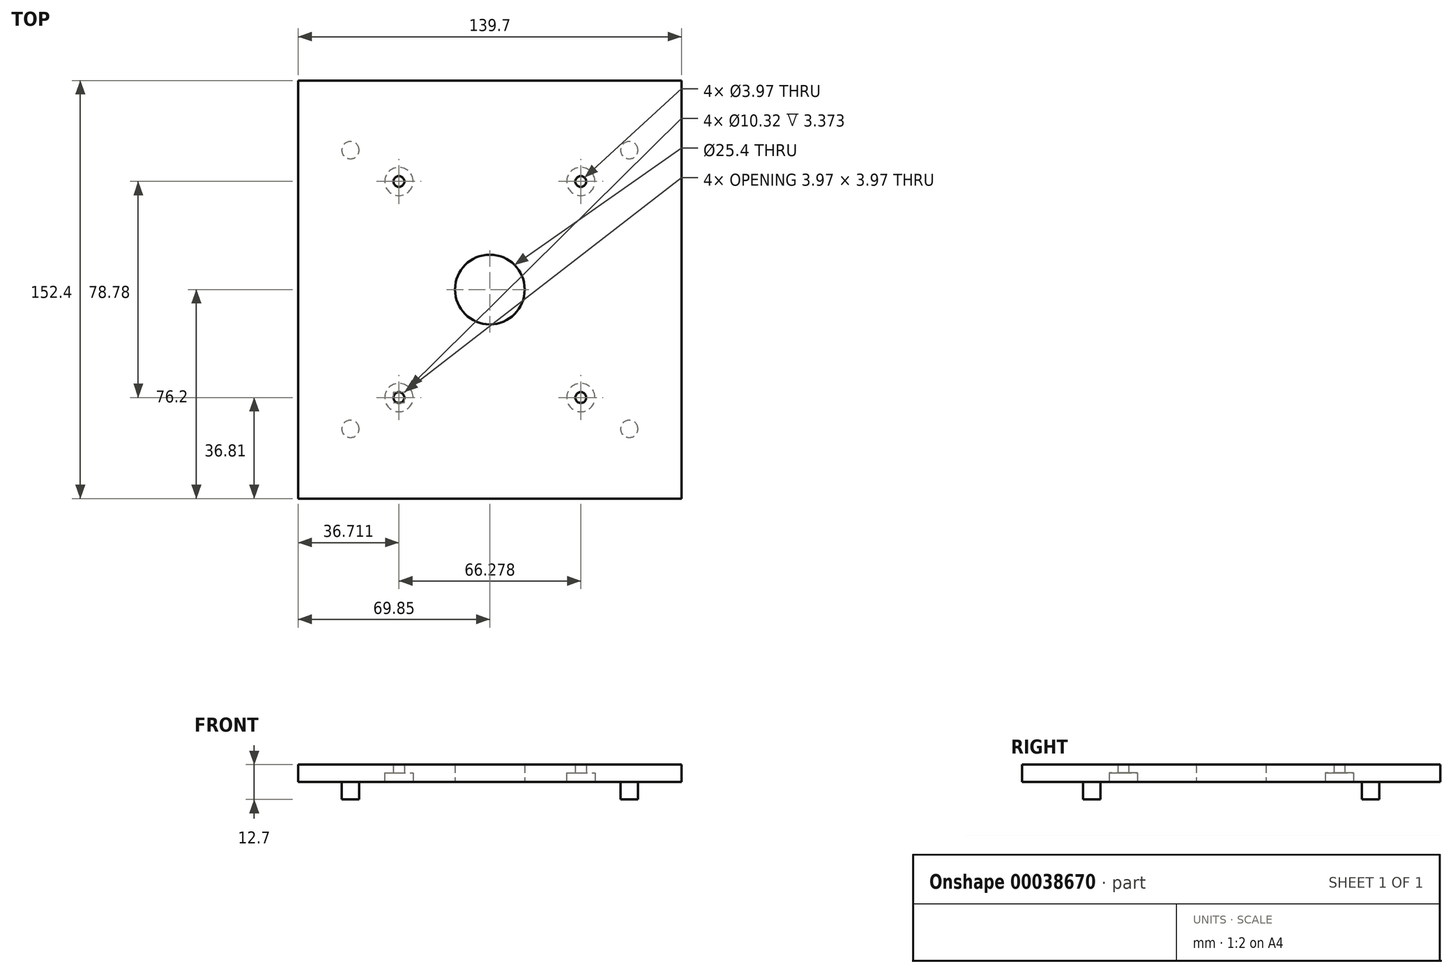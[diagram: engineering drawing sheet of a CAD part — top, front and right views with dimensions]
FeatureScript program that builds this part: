
annotation { "Feature Type Name" : "Feature", "Feature Type Description" : "" }
export const myFeature = defineFeature(function(context is Context, id is Id, definition is map)
    precondition{}
    {
        {
            var Q0;
            Q0=qCreatedBy(makeId("Top.planeOp"),FACE);
            var sketch = newSketch(context, id + "F0", { "sketchPlane" : qUnion([Q0])});
            skLineSegment(sketch, "E0.rect.bottom", {"start": v(33.14, -39.39) * mm, "end": v(-33.14, -39.39) * mm, "construction": true});
            skLineSegment(sketch, "E0.rect.top", {"start": v(33.14, 39.39) * mm, "end": v(-33.14, 39.39) * mm, "construction": true});
            skLineSegment(sketch, "E0.rect.left", {"start": v(33.14, -39.39) * mm, "end": v(33.14, 39.39) * mm, "construction": true});
            skLineSegment(sketch, "E0.rect.right", {"start": v(-33.14, -39.39) * mm, "end": v(-33.14, 39.39) * mm, "construction": true});
            skPoint(sketch, "E0.rect.middle", {"position": v(0, 0) * mm});
            skLineSegment(sketch, "E1.rect.bottom", {"start": v(50.8, 50.8) * mm, "end": v(-50.8, 50.8) * mm, "construction": true});
            skLineSegment(sketch, "E1.rect.top", {"start": v(50.8, -50.8) * mm, "end": v(-50.8, -50.8) * mm, "construction": true});
            skLineSegment(sketch, "E1.rect.left", {"start": v(50.8, 50.8) * mm, "end": v(50.8, -50.8) * mm, "construction": true});
            skLineSegment(sketch, "E1.rect.right", {"start": v(-50.8, 50.8) * mm, "end": v(-50.8, -50.8) * mm, "construction": true});
            skCircle(sketch, "E2", {"center": v(-50.8, 50.8) * mm, "radius": 3.18 * mm});
            skCircle(sketch, "E3", {"center": v(-33.14, -39.39) * mm, "radius": 1.98 * mm});
            skCircle(sketch, "E4", {"center": v(33.14, -39.39) * mm, "radius": 1.98 * mm});
            skCircle(sketch, "E5", {"center": v(-33.14, 39.39) * mm, "radius": 1.98 * mm});
            skCircle(sketch, "E6", {"center": v(0, 0) * mm, "radius": 12.7 * mm});
            skLineSegment(sketch, "E7.rect.bottom", {"start": v(69.85, 76.2) * mm, "end": v(-69.85, 76.2) * mm});
            skLineSegment(sketch, "E7.rect.top", {"start": v(69.85, -76.2) * mm, "end": v(-69.85, -76.2) * mm});
            skLineSegment(sketch, "E7.rect.left", {"start": v(69.85, 76.2) * mm, "end": v(69.85, -76.2) * mm});
            skLineSegment(sketch, "E7.rect.right", {"start": v(-69.85, 76.2) * mm, "end": v(-69.85, -76.2) * mm});
            skCircle(sketch, "E8", {"center": v(33.14, 39.39) * mm, "radius": 1.98 * mm});
            skCircle(sketch, "E9.0.1.0", {"center": v(-50.8, 25.4) * mm, "radius": 3.18 * mm});
            skCircle(sketch, "E9.0.2.0", {"center": v(-50.8, 0) * mm, "radius": 3.18 * mm});
            skCircle(sketch, "E9.0.3.0", {"center": v(-50.8, -25.4) * mm, "radius": 3.18 * mm});
            skCircle(sketch, "E9.0.4.0", {"center": v(-50.8, -50.8) * mm, "radius": 3.18 * mm});
            skCircle(sketch, "E9.1.0.0", {"center": v(-25.4, 50.8) * mm, "radius": 3.18 * mm});
            skCircle(sketch, "E9.1.1.0", {"center": v(-25.4, 25.4) * mm, "radius": 3.18 * mm});
            skCircle(sketch, "E9.1.2.0", {"center": v(-25.4, 0) * mm, "radius": 3.18 * mm});
            skCircle(sketch, "E9.1.3.0", {"center": v(-25.4, -25.4) * mm, "radius": 3.18 * mm});
            skCircle(sketch, "E9.1.4.0", {"center": v(-25.4, -50.8) * mm, "radius": 3.18 * mm});
            skCircle(sketch, "E9.2.0.0", {"center": v(0, 50.8) * mm, "radius": 3.18 * mm});
            skCircle(sketch, "E9.2.1.0", {"center": v(0, 25.4) * mm, "radius": 3.18 * mm});
            skCircle(sketch, "E9.2.2.0", {"center": v(0, 0) * mm, "radius": 3.18 * mm});
            skCircle(sketch, "E9.2.3.0", {"center": v(0, -25.4) * mm, "radius": 3.18 * mm});
            skCircle(sketch, "E9.2.4.0", {"center": v(0, -50.8) * mm, "radius": 3.18 * mm});
            skCircle(sketch, "E9.3.0.0", {"center": v(25.4, 50.8) * mm, "radius": 3.18 * mm});
            skCircle(sketch, "E9.3.1.0", {"center": v(25.4, 25.4) * mm, "radius": 3.18 * mm});
            skCircle(sketch, "E9.3.2.0", {"center": v(25.4, 0) * mm, "radius": 3.18 * mm});
            skCircle(sketch, "E9.3.3.0", {"center": v(25.4, -25.4) * mm, "radius": 3.18 * mm});
            skCircle(sketch, "E9.3.4.0", {"center": v(25.4, -50.8) * mm, "radius": 3.18 * mm});
            skCircle(sketch, "E9.4.0.0", {"center": v(50.8, 50.8) * mm, "radius": 3.18 * mm});
            skCircle(sketch, "E9.4.1.0", {"center": v(50.8, 25.4) * mm, "radius": 3.18 * mm});
            skCircle(sketch, "E9.4.2.0", {"center": v(50.8, 0) * mm, "radius": 3.18 * mm});
            skCircle(sketch, "E9.4.3.0", {"center": v(50.8, -25.4) * mm, "radius": 3.18 * mm});
            skCircle(sketch, "E9.4.4.0", {"center": v(50.8, -50.8) * mm, "radius": 3.18 * mm});
            skLineSegment(sketch, "E9.direction1", {"start": v(-50.8, 50.8) * mm, "end": v(-25.4, 50.8) * mm, "construction": true});
            skLineSegment(sketch, "E9.direction2", {"start": v(-50.8, 50.8) * mm, "end": v(-50.8, 25.4) * mm, "construction": true});
            skSolve(sketch);
        }
        {
            var Q0;
            Q0=makeQuery(id+"F0.imprint","IMPRINT",FACE,{"disambiguationData":[TD([[makeQuery(id+"F0.imprint","IMPRINT",EDGE,{"derivedFrom":sQuery(id+"F0.wireOp",EDGE,"E2")}),-1.0]])]});
            var Q1;
            Q1=makeQuery(id+"F0.imprint","IMPRINT",FACE,{"disambiguationData":[TD([[makeQuery(id+"F0.imprint","IMPRINT",EDGE,{"derivedFrom":sQuery(id+"F0.wireOp",EDGE,"E9.1.0.0")}),1.0]])]});
            var Q2;
            Q2=makeQuery(id+"F0.imprint","IMPRINT",FACE,{"disambiguationData":[TD([[makeQuery(id+"F0.imprint","IMPRINT",EDGE,{"derivedFrom":sQuery(id+"F0.wireOp",EDGE,"E9.2.0.0")}),1.0]])]});
            var Q3;
            Q3=makeQuery(id+"F0.imprint","IMPRINT",FACE,{"disambiguationData":[TD([[makeQuery(id+"F0.imprint","IMPRINT",EDGE,{"derivedFrom":sQuery(id+"F0.wireOp",EDGE,"E9.3.0.0")}),1.0]])]});
            var Q4;
            Q4=makeQuery(id+"F0.imprint","IMPRINT",FACE,{"disambiguationData":[TD([[makeQuery(id+"F0.imprint","IMPRINT",EDGE,{"derivedFrom":sQuery(id+"F0.wireOp",EDGE,"E9.4.1.0")}),1.0]])]});
            var Q5;
            Q5=makeQuery(id+"F0.imprint","IMPRINT",FACE,{"disambiguationData":[TD([[makeQuery(id+"F0.imprint","IMPRINT",EDGE,{"derivedFrom":sQuery(id+"F0.wireOp",EDGE,"E9.4.2.0")}),1.0]])]});
            var Q6;
            Q6=makeQuery(id+"F0.imprint","IMPRINT",FACE,{"disambiguationData":[TD([[makeQuery(id+"F0.imprint","IMPRINT",EDGE,{"derivedFrom":sQuery(id+"F0.wireOp",EDGE,"E9.4.3.0")}),1.0]])]});
            var Q7;
            Q7=makeQuery(id+"F0.imprint","IMPRINT",FACE,{"disambiguationData":[TD([[makeQuery(id+"F0.imprint","IMPRINT",EDGE,{"derivedFrom":sQuery(id+"F0.wireOp",EDGE,"E9.3.4.0")}),1.0]])]});
            var Q8;
            Q8=makeQuery(id+"F0.imprint","IMPRINT",FACE,{"disambiguationData":[TD([[makeQuery(id+"F0.imprint","IMPRINT",EDGE,{"derivedFrom":sQuery(id+"F0.wireOp",EDGE,"E9.2.4.0")}),1.0]])]});
            var Q9;
            Q9=makeQuery(id+"F0.imprint","IMPRINT",FACE,{"disambiguationData":[TD([[makeQuery(id+"F0.imprint","IMPRINT",EDGE,{"derivedFrom":sQuery(id+"F0.wireOp",EDGE,"E9.1.4.0")}),1.0]])]});
            var Q10;
            Q10=makeQuery(id+"F0.imprint","IMPRINT",FACE,{"disambiguationData":[TD([[makeQuery(id+"F0.imprint","IMPRINT",EDGE,{"derivedFrom":sQuery(id+"F0.wireOp",EDGE,"E9.0.3.0")}),1.0]])]});
            var Q11;
            Q11=makeQuery(id+"F0.imprint","IMPRINT",FACE,{"disambiguationData":[TD([[makeQuery(id+"F0.imprint","IMPRINT",EDGE,{"derivedFrom":sQuery(id+"F0.wireOp",EDGE,"E9.0.2.0")}),1.0]])]});
            var Q12;
            Q12=makeQuery(id+"F0.imprint","IMPRINT",FACE,{"disambiguationData":[TD([[makeQuery(id+"F0.imprint","IMPRINT",EDGE,{"derivedFrom":sQuery(id+"F0.wireOp",EDGE,"E9.0.1.0")}),1.0]])]});
            var Q13;
            Q13=makeQuery(id+"F0.imprint","IMPRINT",FACE,{"disambiguationData":[TD([[makeQuery(id+"F0.imprint","IMPRINT",EDGE,{"derivedFrom":sQuery(id+"F0.wireOp",EDGE,"E9.1.1.0")}),1.0]])]});
            var Q14;
            Q14=makeQuery(id+"F0.imprint","IMPRINT",FACE,{"disambiguationData":[TD([[makeQuery(id+"F0.imprint","IMPRINT",EDGE,{"derivedFrom":sQuery(id+"F0.wireOp",EDGE,"E9.2.1.0")}),1.0]])]});
            var Q15;
            Q15=makeQuery(id+"F0.imprint","IMPRINT",FACE,{"disambiguationData":[TD([[makeQuery(id+"F0.imprint","IMPRINT",EDGE,{"derivedFrom":sQuery(id+"F0.wireOp",EDGE,"E9.3.1.0")}),1.0]])]});
            var Q16;
            Q16=makeQuery(id+"F0.imprint","IMPRINT",FACE,{"disambiguationData":[TD([[makeQuery(id+"F0.imprint","IMPRINT",EDGE,{"derivedFrom":sQuery(id+"F0.wireOp",EDGE,"E9.3.2.0")}),1.0]])]});
            var Q17;
            Q17=makeQuery(id+"F0.imprint","IMPRINT",FACE,{"disambiguationData":[TD([[makeQuery(id+"F0.imprint","IMPRINT",EDGE,{"derivedFrom":sQuery(id+"F0.wireOp",EDGE,"E9.3.3.0")}),1.0]])]});
            var Q18;
            Q18=makeQuery(id+"F0.imprint","IMPRINT",FACE,{"disambiguationData":[TD([[makeQuery(id+"F0.imprint","IMPRINT",EDGE,{"derivedFrom":sQuery(id+"F0.wireOp",EDGE,"E9.2.3.0")}),1.0]])]});
            var Q19;
            Q19=makeQuery(id+"F0.imprint","IMPRINT",FACE,{"disambiguationData":[TD([[makeQuery(id+"F0.imprint","IMPRINT",EDGE,{"derivedFrom":sQuery(id+"F0.wireOp",EDGE,"E9.1.2.0")}),1.0]])]});
            var Q20;
            Q20=makeQuery(id+"F0.imprint","IMPRINT",FACE,{"disambiguationData":[TD([[makeQuery(id+"F0.imprint","IMPRINT",EDGE,{"derivedFrom":sQuery(id+"F0.wireOp",EDGE,"E9.1.3.0")}),1.0]])]});
            extrude(context, id + "F1", {"entities" : qUnion([Q0, Q1, Q2, Q3, Q4, Q5, Q6, Q7, Q8, Q9, Q10, Q11, Q12, Q13, Q14, Q15, Q16, Q17, Q18, Q19, Q20]), "depth" : 6.35 * mm});
        }
        {
            var Q0;
            Q0=makeQuery(id+"F1.opExtrude","CAP_FACE",FACE,{"disambiguationData":[OSD([sQuery(id+"F0.wireOp",EDGE,"E2"),sQuery(id+"F0.wireOp",EDGE,"E3"),sQuery(id+"F0.wireOp",EDGE,"E4"),sQuery(id+"F0.wireOp",EDGE,"E5"),sQuery(id+"F0.wireOp",EDGE,"E6"),sQuery(id+"F0.wireOp",EDGE,"E7.rect.bottom"),sQuery(id+"F0.wireOp",EDGE,"E7.rect.top"),sQuery(id+"F0.wireOp",EDGE,"E7.rect.left"),sQuery(id+"F0.wireOp",EDGE,"E7.rect.right"),sQuery(id+"F0.wireOp",EDGE,"E8"),sQuery(id+"F0.wireOp",EDGE,"E9.0.4.0"),sQuery(id+"F0.wireOp",EDGE,"E9.4.0.0"),sQuery(id+"F0.wireOp",EDGE,"E9.4.4.0")])],"isStart":false});
            var sketch = newSketch(context, id + "F2", { "sketchPlane" : qUnion([Q0])});
            skCircle(sketch, "E10.0", {"center": v(33.14, -39.39) * mm, "radius": 1.98 * mm, "construction": true});
            skCircle(sketch, "E11.0", {"center": v(-33.14, -39.39) * mm, "radius": 1.98 * mm, "construction": true});
            skCircle(sketch, "E12.0", {"center": v(-33.14, 39.39) * mm, "radius": 1.98 * mm, "construction": true});
            skCircle(sketch, "E13.0", {"center": v(33.14, 39.39) * mm, "radius": 1.98 * mm, "construction": true});
            skSolve(sketch);
        }
        {
            var Q0;
            Q0 = qSketchRegion(id + "F2", true);
            var Q1;
            Q1=makeQuery(id+"F2.imprint","IMPRINT",FACE,{"disambiguationData":[TD([[makeQuery(id+"F2.imprint","IMPRINT",EDGE,{"derivedFrom":makeQuery(id+"F1.opExtrude","CAP_EDGE",EDGE,{"disambiguationData":[OSD([sQuery(id+"F0.wireOp",EDGE,"E9.4.4.0")])],"isStart":false})}),1.0]])]});
            var Q2;
            Q2=makeQuery(id+"F2.imprint","IMPRINT",FACE,{"disambiguationData":[TD([[makeQuery(id+"F2.imprint","IMPRINT",EDGE,{"derivedFrom":makeQuery(id+"F1.opExtrude","CAP_EDGE",EDGE,{"disambiguationData":[OSD([sQuery(id+"F0.wireOp",EDGE,"E9.0.4.0")])],"isStart":false})}),1.0]])]});
            var Q3;
            Q3=makeQuery(id+"F2.imprint","IMPRINT",FACE,{"disambiguationData":[TD([[makeQuery(id+"F2.imprint","IMPRINT",EDGE,{"derivedFrom":makeQuery(id+"F1.opExtrude","CAP_EDGE",EDGE,{"disambiguationData":[OSD([sQuery(id+"F0.wireOp",EDGE,"E2")])],"isStart":false})}),1.0]])]});
            var Q4;
            Q4=makeQuery(id+"F2.imprint","IMPRINT",FACE,{"disambiguationData":[TD([[makeQuery(id+"F2.imprint","IMPRINT",EDGE,{"derivedFrom":makeQuery(id+"F1.opExtrude","CAP_EDGE",EDGE,{"disambiguationData":[OSD([sQuery(id+"F0.wireOp",EDGE,"E9.4.0.0")])],"isStart":false})}),1.0]])]});
            extrude(context, id + "F3", {"entities" : qUnion([Q0, Q1, Q2, Q3, Q4]), "operationType" : NewBodyOperationType.ADD, "oppositeDirection" : true, "depth" : 12.7 * mm});
        }
        {
            var Q0;
            Q0=makeQuery(id+"F1.opExtrude","CAP_FACE",FACE,{"disambiguationData":[OSD([sQuery(id+"F0.wireOp",EDGE,"E2"),sQuery(id+"F0.wireOp",EDGE,"E3"),sQuery(id+"F0.wireOp",EDGE,"E4"),sQuery(id+"F0.wireOp",EDGE,"E5"),sQuery(id+"F0.wireOp",EDGE,"E6"),sQuery(id+"F0.wireOp",EDGE,"E7.rect.bottom"),sQuery(id+"F0.wireOp",EDGE,"E7.rect.top"),sQuery(id+"F0.wireOp",EDGE,"E7.rect.left"),sQuery(id+"F0.wireOp",EDGE,"E7.rect.right"),sQuery(id+"F0.wireOp",EDGE,"E8"),sQuery(id+"F0.wireOp",EDGE,"E9.0.4.0"),sQuery(id+"F0.wireOp",EDGE,"E9.4.0.0"),sQuery(id+"F0.wireOp",EDGE,"E9.4.4.0")])],"isStart":true});
            var sketch = newSketch(context, id + "F4", { "sketchPlane" : qUnion([Q0])});
            skCircle(sketch, "E14.0", {"center": v(-33.14, 39.39) * mm, "radius": 1.98 * mm});
            skCircle(sketch, "E15.0", {"center": v(33.14, 39.39) * mm, "radius": 1.98 * mm});
            skCircle(sketch, "E16.0", {"center": v(-33.14, -39.39) * mm, "radius": 1.98 * mm});
            skCircle(sketch, "E17.0", {"center": v(33.14, -39.39) * mm, "radius": 1.98 * mm});
            skSolve(sketch);
        }
        {
            var Q0;
            Q0=sQuery(id+"F4.wireOp",VERTEX,"E14.0.center");
            var Q1;
            Q1=sQuery(id+"F4.wireOp",VERTEX,"E15.0.center");
            var Q2;
            Q2=sQuery(id+"F4.wireOp",VERTEX,"E17.0.center");
            var Q3;
            Q3=sQuery(id+"F4.wireOp",VERTEX,"E16.0.center");
            var Q4;
            Q4=makeQuery(id+"F1.opExtrude","SWEPT_BODY",BODY,{"disambiguationData":[OSD([sQuery(id+"F0.wireOp",EDGE,"E2"),sQuery(id+"F0.wireOp",EDGE,"E3"),sQuery(id+"F0.wireOp",EDGE,"E4"),sQuery(id+"F0.wireOp",EDGE,"E5"),sQuery(id+"F0.wireOp",EDGE,"E6"),sQuery(id+"F0.wireOp",EDGE,"E7.rect.bottom"),sQuery(id+"F0.wireOp",EDGE,"E7.rect.top"),sQuery(id+"F0.wireOp",EDGE,"E7.rect.left"),sQuery(id+"F0.wireOp",EDGE,"E7.rect.right"),sQuery(id+"F0.wireOp",EDGE,"E8"),sQuery(id+"F0.wireOp",EDGE,"E9.0.4.0"),sQuery(id+"F0.wireOp",EDGE,"E9.4.0.0"),sQuery(id+"F0.wireOp",EDGE,"E9.4.4.0")])]});
            hole(context, id + "F5", {"style" : HoleStyle.C_BORE, "holeDiameter" : 3.96 * mm, "cBoreDiameter" : 10.32 * mm, "cBoreDepth" : 3.37 * mm, "endStyle" : HoleEndStyle.THROUGH, "locations" : qUnion([Q0, Q1, Q2, Q3]), "scope" : qUnion([Q4])});
        }
    });
